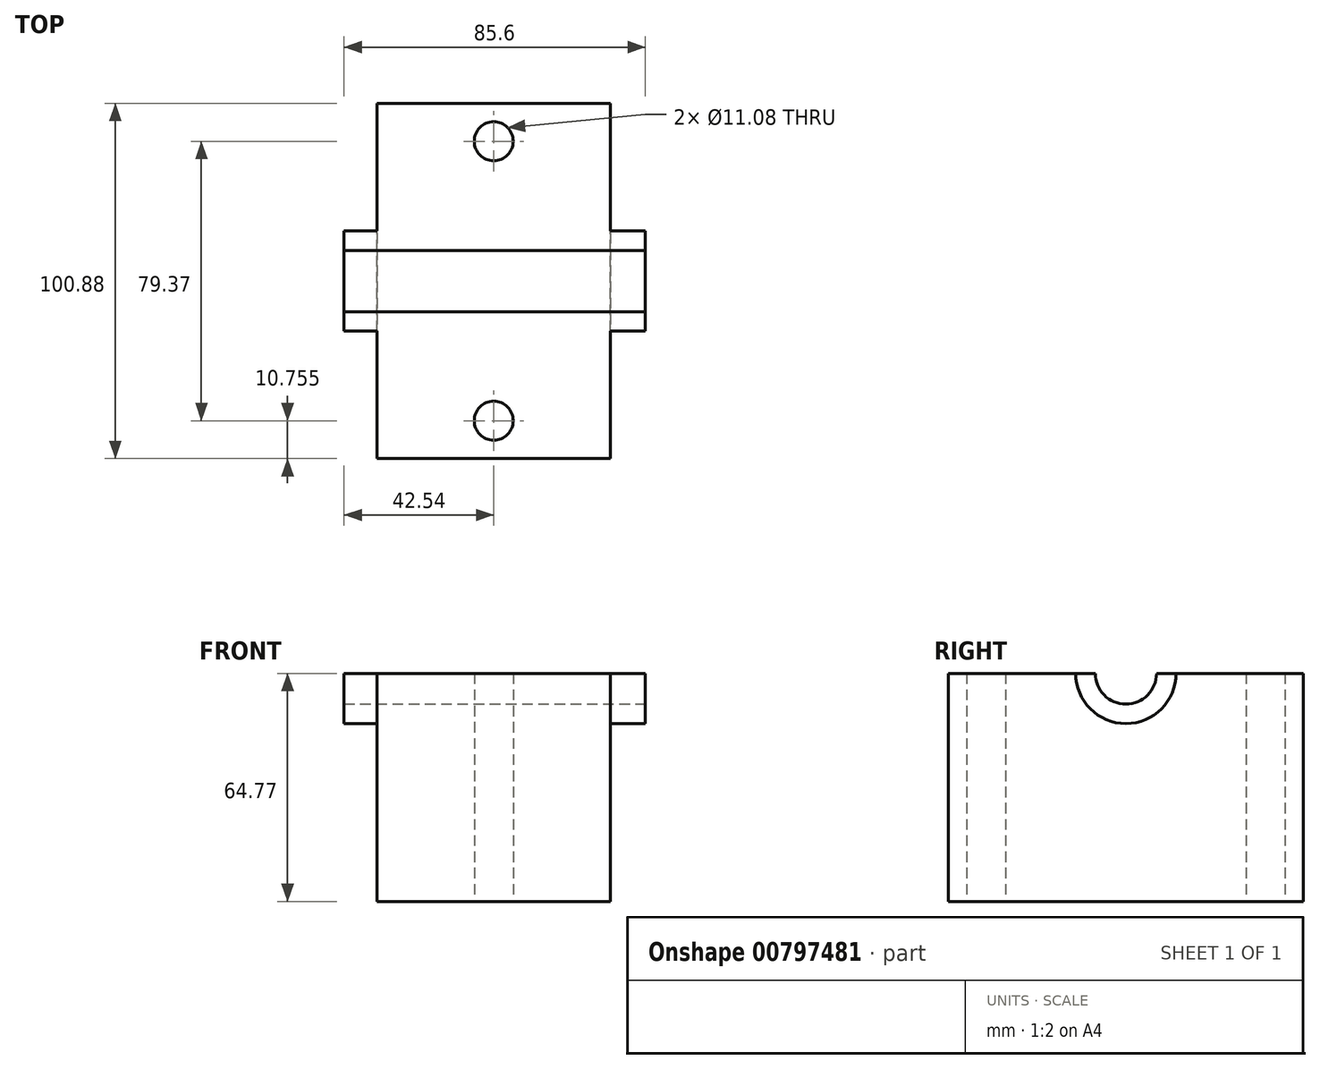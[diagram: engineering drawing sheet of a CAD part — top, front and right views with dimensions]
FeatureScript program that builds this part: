
annotation { "Feature Type Name" : "Feature", "Feature Type Description" : "" }
export const myFeature = defineFeature(function(context is Context, id is Id, definition is map)
    precondition{}
    {
        {
            var Q0;
            Q0=qCreatedBy(makeId("Top.planeOp"),FACE);
            var sketch = newSketch(context, id + "F0", { "sketchPlane" : qUnion([Q0])});
            skLineSegment(sketch, "E0.bottom", {"start": v(-33.16, 50.44) * mm, "end": v(33.16, 50.44) * mm});
            skLineSegment(sketch, "E0.top", {"start": v(-33.16, -50.44) * mm, "end": v(33.16, -50.44) * mm});
            skLineSegment(sketch, "E0.left", {"start": v(-33.16, 50.44) * mm, "end": v(-33.16, -50.44) * mm});
            skLineSegment(sketch, "E0.right", {"start": v(33.16, 50.44) * mm, "end": v(33.16, -50.44) * mm});
            skPoint(sketch, "E0.middle", {"position": v(0, 0) * mm});
            skCircle(sketch, "E1", {"center": v(0, 39.68) * mm, "radius": 5.54 * mm});
            skCircle(sketch, "E2.MirrorC", {"center": v(0, -39.68) * mm, "radius": 5.54 * mm});
            skSolve(sketch);
        }
        {
            var Q0;
            Q0 = qSketchRegion(id + "F0", true);
            extrude(context, id + "F1", {"entities" : qUnion([Q0]), "depth" : 64.77 * mm, "offsetDistance" : 25.4 * mm});
        }
        {
            var Q0;
            Q0=makeQuery(id+"F1.opExtrude","SWEPT_FACE",FACE,{"disambiguationData":[OSD([sQuery(id+"F0.wireOp",EDGE,"E0.right")])]});
            var sketch = newSketch(context, id + "F2", { "sketchPlane" : qUnion([Q0])});
            skArc(sketch, "E3", {"start": v(-8.48, 64.77) * mm, "mid": v(0, 56.3) * mm, "end": v(8.48, 64.77) * mm});
            skArc(sketch, "E4", {"start": v(-14.27, 64.77) * mm, "mid": v(0, 50.5) * mm, "end": v(14.27, 64.77) * mm});
            skLineSegment(sketch, "E5", {"start": v(-8.48, 64.77) * mm, "end": v(-14.27, 64.77) * mm});
            skLineSegment(sketch, "E6", {"start": v(-14.27, 64.77) * mm, "end": v(-8.48, 64.77) * mm});
            skLineSegment(sketch, "E7", {"start": v(8.48, 64.77) * mm, "end": v(14.27, 64.77) * mm});
            skLineSegment(sketch, "E8", {"start": v(14.27, 64.77) * mm, "end": v(8.48, 64.77) * mm});
            skLineSegment(sketch, "E9", {"start": v(-8.48, 64.77) * mm, "end": v(8.48, 64.77) * mm});
            skSolve(sketch);
        }
        {
            var Q0;
            Q0 = qSketchRegion(id + "F2", true);
            extrude(context, id + "F3", {"entities" : qUnion([Q0]), "operationType" : NewBodyOperationType.ADD, "endBound" : BoundingType.SYMMETRIC, "oppositeDirection" : true, "depth" : 151.38 * mm, "offsetDistance" : 25.4 * mm});
        }
        {
            var Q0;
            Q0=makeQuery(id+"F3.opExtrude","CAP_FACE",FACE,{"disambiguationData":[OSD([sQuery(id+"F2.wireOp",EDGE,"E4"),sQuery(id+"F2.wireOp",EDGE,"E6"),sQuery(id+"F2.wireOp",EDGE,"E8"),sQuery(id+"F2.wireOp",EDGE,"E9")])],"isStart":true});
            var sketch = newSketch(context, id + "F4", { "sketchPlane" : qUnion([Q0])});
            skSolve(sketch);
        }
        {
            var Q0;
            Q0 = qSketchRegion(id + "F4", true);
            var Q1;
            Q1=makeQuery(id+"F4.imprint","IMPRINT",FACE,{"disambiguationData":[TD([[makeQuery(id+"F4.imprint","IMPRINT",EDGE,{"derivedFrom":makeQuery(id+"F3.opExtrude","CAP_EDGE",EDGE,{"disambiguationData":[OSD([sQuery(id+"F2.wireOp",EDGE,"E4")])],"isStart":true})}),1.0]])]});
            extrude(context, id + "F5", {"entities" : qUnion([Q0, Q1]), "operationType" : NewBodyOperationType.REMOVE, "oppositeDirection" : true, "depth" : 65.8 * mm, "offsetDistance" : 25.4 * mm});
        }
        {
            var Q0;
            Q0=makeQuery(id+"F5.boolean.opBoolean","COPY",FACE,{"derivedFrom":makeQuery(id+"F5.opExtrude","CAP_FACE",FACE,{"disambiguationData":[OSD([sQuery(id+"F2.wireOp",EDGE,"E4"),sQuery(id+"F2.wireOp",EDGE,"E6"),sQuery(id+"F2.wireOp",EDGE,"E8"),sQuery(id+"F2.wireOp",EDGE,"E9")])],"isStart":false})});
            var sketch = newSketch(context, id + "F6", { "sketchPlane" : qUnion([Q0])});
            skArc(sketch, "E10", {"start": v(-8.71, 64.77) * mm, "mid": v(0, 56.06) * mm, "end": v(8.71, 64.77) * mm});
            skSolve(sketch);
        }
        {
            var Q0;
            Q0 = qSketchRegion(id + "F6", true);
            var Q1;
            {var subQ0=sQuery(id+"F6.wireOp",EDGE,"E10");Q1=makeQuery(id+"F6.imprint","IMPRINT",FACE,{"disambiguationData":[TD([[makeQuery(id+"F6.imprint","IMPRINT",EDGE,{"derivedFrom":subQ0}),1.0]])]});}
            extrude(context, id + "F7", {"entities" : qUnion([Q0, Q1]), "operationType" : NewBodyOperationType.REMOVE, "oppositeDirection" : true, "depth" : 101.6 * mm, "offsetDistance" : 25.4 * mm});
        }
    });
